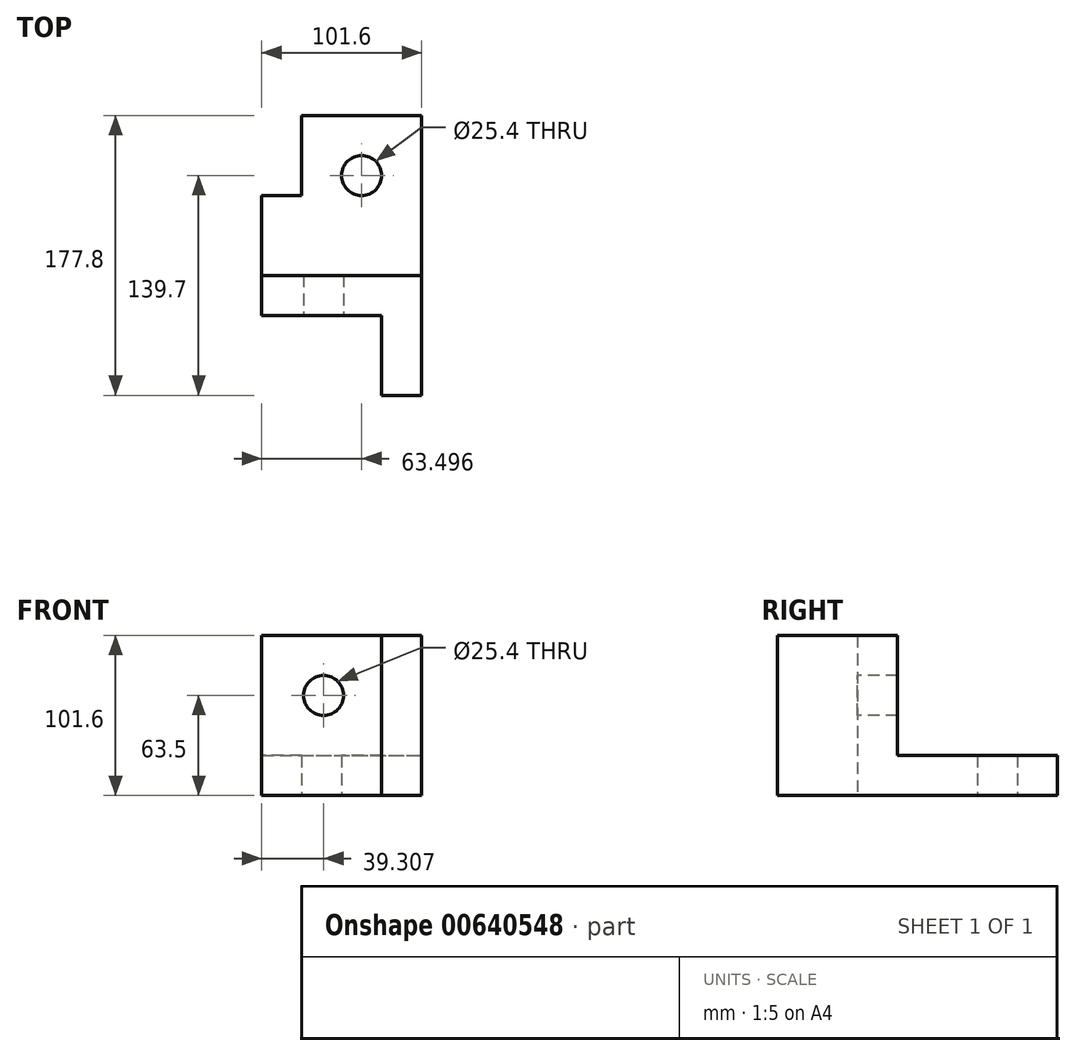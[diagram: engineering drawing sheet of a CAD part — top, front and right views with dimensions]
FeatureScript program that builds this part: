
annotation { "Feature Type Name" : "Feature", "Feature Type Description" : "" }
export const myFeature = defineFeature(function(context is Context, id is Id, definition is map)
    precondition{}
    {
        {
            var Q0;
            Q0=qCreatedBy(makeId("Top.planeOp"),FACE);
            var sketch = newSketch(context, id + "F0", { "sketchPlane" : qUnion([Q0])});
            skLineSegment(sketch, "E0.bottom", {"start": v(-73.4, 78.12) * mm, "end": v(2.8, 78.12) * mm});
            skLineSegment(sketch, "E0.top", {"start": v(-73.4, -48.88) * mm, "end": v(-22.6, -48.88) * mm});
            skLineSegment(sketch, "E0.left", {"start": v(-73.4, 78.12) * mm, "end": v(-73.4, 27.32) * mm});
            skLineSegment(sketch, "E0.right", {"start": v(2.8, 78.12) * mm, "end": v(2.8, -48.88) * mm});
            skLineSegment(sketch, "E1.bottom", {"start": v(-73.4, -48.88) * mm, "end": v(-98.8, -48.88) * mm});
            skLineSegment(sketch, "E1.top", {"start": v(-73.4, 27.32) * mm, "end": v(-98.8, 27.32) * mm});
            skLineSegment(sketch, "E1.right", {"start": v(-98.8, -48.88) * mm, "end": v(-98.8, 27.32) * mm});
            skCircle(sketch, "E2", {"center": v(-35.3, 40.02) * mm, "radius": 12.7 * mm});
            skLineSegment(sketch, "E3.top", {"start": v(2.8, -99.68) * mm, "end": v(-22.6, -99.68) * mm});
            skLineSegment(sketch, "E3.left", {"start": v(2.8, -48.88) * mm, "end": v(2.8, -99.68) * mm});
            skLineSegment(sketch, "E3.right", {"start": v(-22.6, -48.88) * mm, "end": v(-22.6, -99.68) * mm});
            skSolve(sketch);
        }
        {
            var Q0;
            Q0 = qSketchRegion(id + "F0", true);
            extrude(context, id + "F1", {"entities" : qUnion([Q0]), "depth" : 25.4 * mm, "offsetDistance" : 25.4 * mm});
        }
        {
            var Q0;
            Q0=makeQuery(id+"F1.opExtrude","CAP_FACE",FACE,{"disambiguationData":[OSD([sQuery(id+"F0.wireOp",EDGE,"E0.bottom"),sQuery(id+"F0.wireOp",EDGE,"E0.top"),sQuery(id+"F0.wireOp",EDGE,"E0.left"),sQuery(id+"F0.wireOp",EDGE,"E0.right"),sQuery(id+"F0.wireOp",EDGE,"E1.bottom"),sQuery(id+"F0.wireOp",EDGE,"E1.top"),sQuery(id+"F0.wireOp",EDGE,"E1.right"),sQuery(id+"F0.wireOp",EDGE,"E2"),sQuery(id+"F0.wireOp",EDGE,"E3.top"),sQuery(id+"F0.wireOp",EDGE,"E3.left"),sQuery(id+"F0.wireOp",EDGE,"E3.right")])],"isStart":false});
            var sketch = newSketch(context, id + "F2", { "sketchPlane" : qUnion([Q0])});
            skLineSegment(sketch, "E4", {"start": v(-98.8, -23.48) * mm, "end": v(2.8, -23.48) * mm});
            skSolve(sketch);
        }
        {
            var Q0;
            Q0 = qSketchRegion(id + "F2", true);
            var Q1;
            {var subQ2=sQuery(id+"F2.wireOp",EDGE,"E4");Q1=makeQuery(id+"F2.imprint","IMPRINT",FACE,{"disambiguationData":[TD([[makeQuery(id+"F2.imprint","IMPRINT",EDGE,{"derivedFrom":subQ2}),-1.0]])]});}
            extrude(context, id + "F3", {"entities" : qUnion([Q0, Q1]), "operationType" : NewBodyOperationType.ADD, "depth" : 76.2 * mm, "offsetDistance" : 25.4 * mm});
        }
        {
            var Q0;
            {var subQ0=sQuery(id+"F0.wireOp",EDGE,"E1.bottom");var subQ1=sQuery(id+"F0.wireOp",EDGE,"E0.top");Q0=makeQuery(id+"F3.boolean.opBoolean","MERGE",FACE,{"derivedFrom":[makeQuery(id+"F1.opExtrude","SWEPT_FACE",FACE,{"disambiguationData":[OSD([subQ1,subQ0])]}),makeQuery(id+"F3.opExtrude","SWEPT_FACE",FACE,{"disambiguationData":[OSD([subQ1,subQ0])]})]});}
            var sketch = newSketch(context, id + "F4", { "sketchPlane" : qUnion([Q0])});
            skCircle(sketch, "E5", {"center": v(-59.48, 63.5) * mm, "radius": 12.7 * mm});
            skSolve(sketch);
        }
        {
            var Q0;
            Q0 = qSketchRegion(id + "F4", true);
            extrude(context, id + "F5", {"entities" : qUnion([Q0]), "operationType" : NewBodyOperationType.REMOVE, "oppositeDirection" : true, "depth" : 25.4 * mm, "offsetDistance" : 25.4 * mm});
        }
    });
